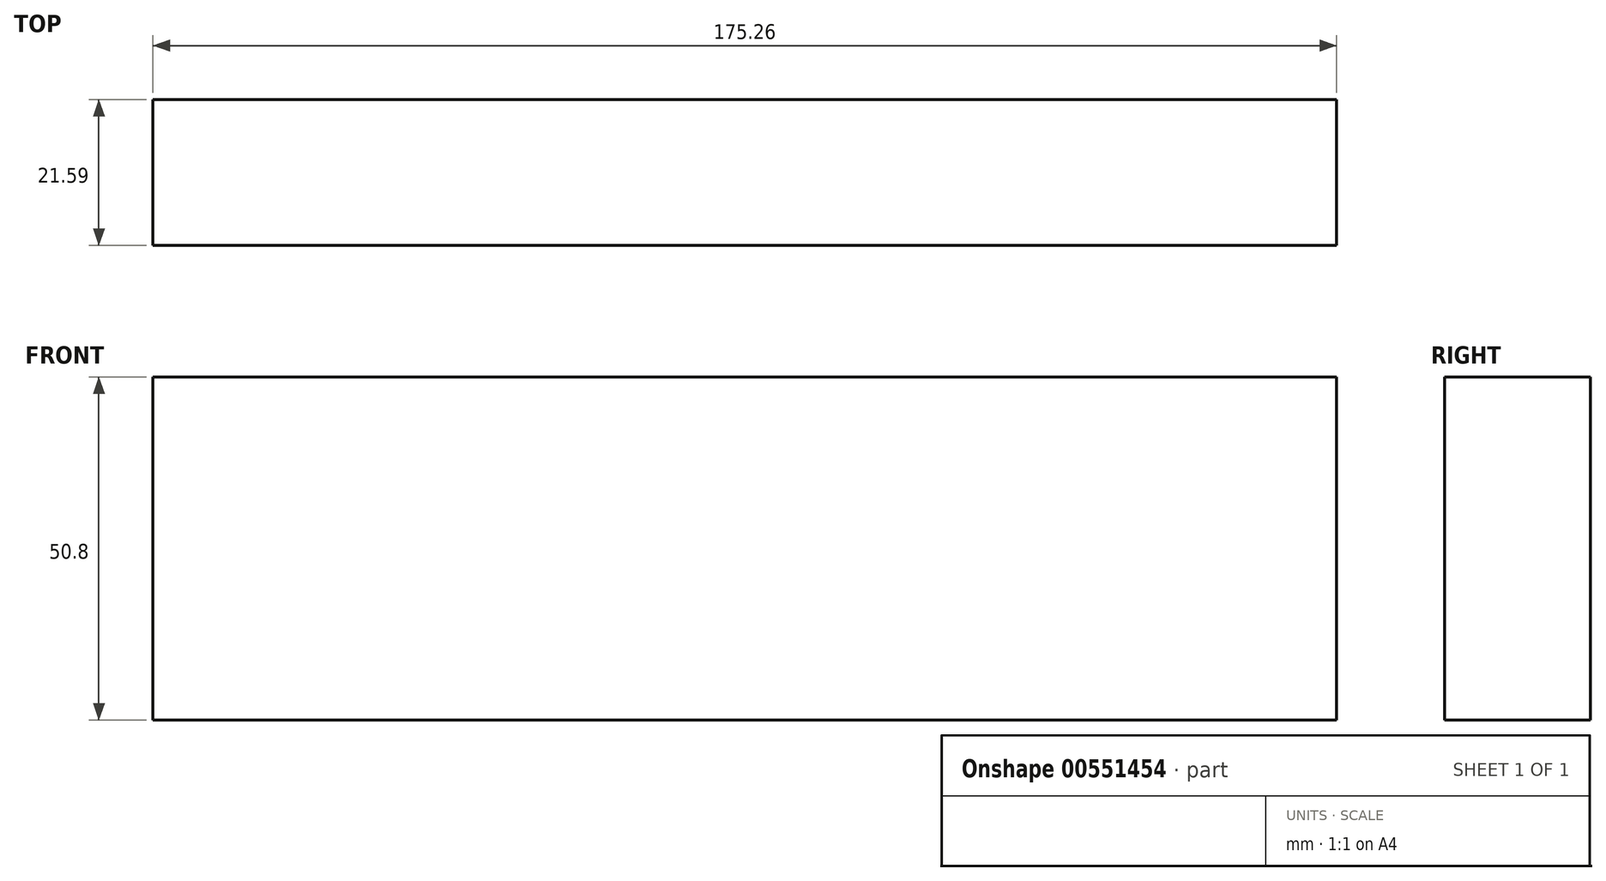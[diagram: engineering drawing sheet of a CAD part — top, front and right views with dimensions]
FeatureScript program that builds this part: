
annotation { "Feature Type Name" : "Feature", "Feature Type Description" : "" }
export const myFeature = defineFeature(function(context is Context, id is Id, definition is map)
    precondition{}
    {
        {
            var Q0;
            Q0=qCreatedBy(makeId("Front.planeOp"),FACE);
            var sketch = newSketch(context, id + "F0", { "sketchPlane" : qUnion([Q0])});
            skLineSegment(sketch, "E0.bottom", {"start": v(87.63, 25.4) * mm, "end": v(-87.63, 25.4) * mm});
            skLineSegment(sketch, "E0.top", {"start": v(87.63, -25.4) * mm, "end": v(-87.63, -25.4) * mm});
            skLineSegment(sketch, "E0.left", {"start": v(87.63, 25.4) * mm, "end": v(87.63, -25.4) * mm});
            skLineSegment(sketch, "E0.right", {"start": v(-87.63, 25.4) * mm, "end": v(-87.63, -25.4) * mm});
            skPoint(sketch, "E0.middle", {"position": v(0, 0) * mm});
            skSolve(sketch);
        }
        {
            var Q0;
            Q0 = qSketchRegion(id + "F0", true);
            extrude(context, id + "F1", {"entities" : qUnion([Q0]), "depth" : 21.59 * mm, "offsetDistance" : 25.4 * mm});
        }
    });
